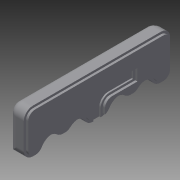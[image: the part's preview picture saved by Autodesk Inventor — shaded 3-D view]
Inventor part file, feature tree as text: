
AUTODESK INVENTOR PART (.ipt)
format: ipt  version: 2015 (Build 190159000, 159)  size: 201,216 bytes
history: native  units: in
note: dims shown in document units (in); Inventor stores cm internally (conversion verified against a paired STEP export)
features: extrude x2, sketch x2, fillet x1, other x1, projected_geometry x1
ambient origin geometry x8: Origin, YZ Plane, XZ Plane, XY Plane, X Axis, Y Axis, Z Axis, Center Point
bodies: Solid1 (feature_tree)
feature tree (7):
  extrude  "Extrusion1"  Depth=2.0in
  extrude  "Extrusion2"  Depth=0.1in
  fillet  "Fillet1"  Radius=0.125in
  other  "Lip1"
  sketch  "Sketch1"  dims[d0=0.6in d1=2.0in]
  sketch  "Sketch2"  dims[d2=0.25in d3=0.0in d4=0.1in d5=0.125in d6=0.05in d7=0.0in d8=0.125in d9=0.03in d10=0.03in d11=0.0in d12=0.0in d13=0.0in d14=0.0in]
  projected_geometry  "Projected Loop1"
